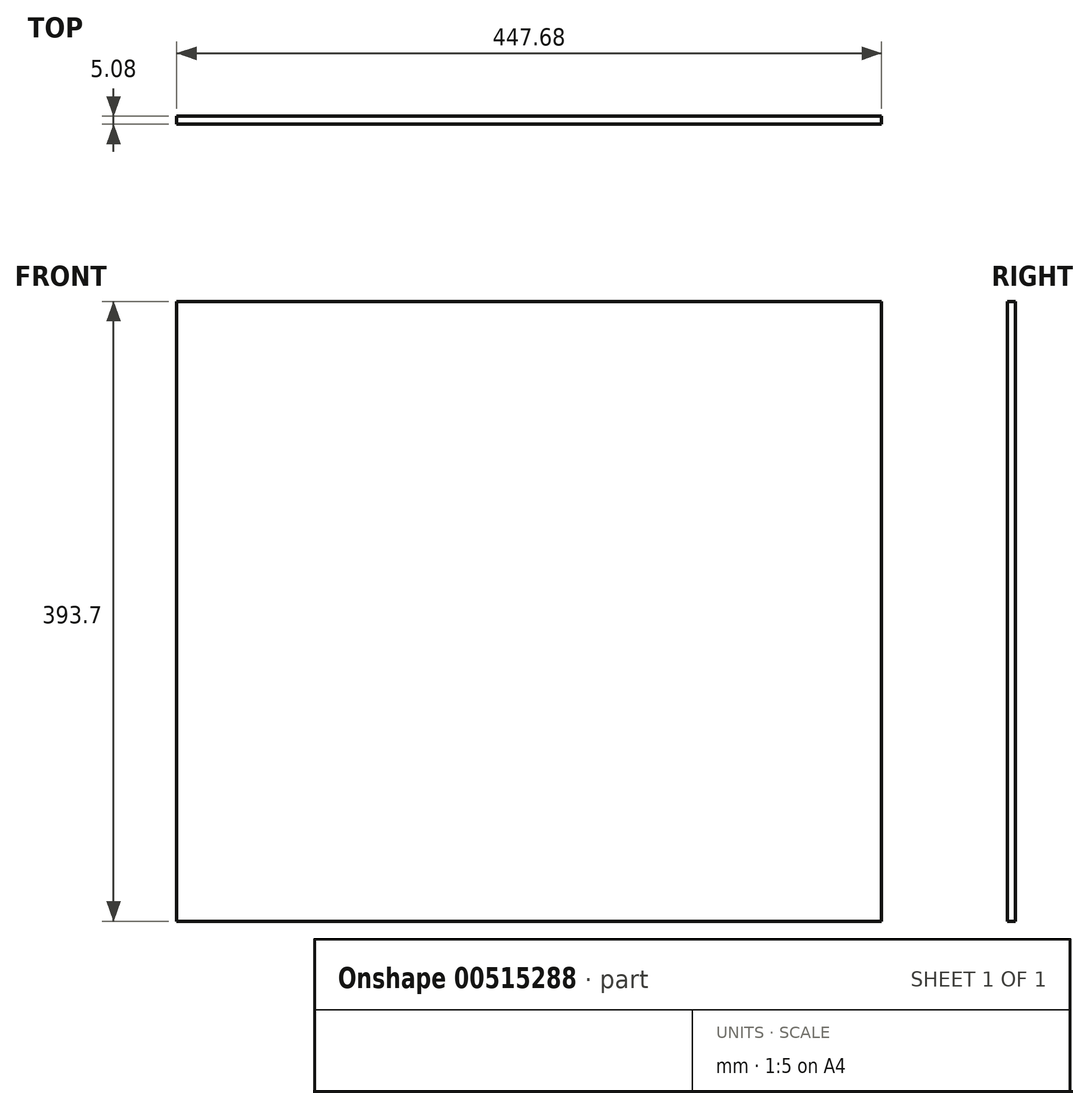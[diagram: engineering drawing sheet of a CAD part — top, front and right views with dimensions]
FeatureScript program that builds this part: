
annotation { "Feature Type Name" : "Feature", "Feature Type Description" : "" }
export const myFeature = defineFeature(function(context is Context, id is Id, definition is map)
    precondition{}
    {
        {
            var Q0;
            Q0=qCreatedBy(makeId("Front.planeOp"),FACE);
            var sketch = newSketch(context, id + "F0", { "sketchPlane" : qUnion([Q0])});
            skLineSegment(sketch, "E0.bottom", {"start": v(-525.36, 360.57) * mm, "end": v(-77.68, 360.57) * mm});
            skLineSegment(sketch, "E0.top", {"start": v(-525.36, -33.13) * mm, "end": v(-77.68, -33.13) * mm});
            skLineSegment(sketch, "E0.left", {"start": v(-525.36, 360.57) * mm, "end": v(-525.36, -33.13) * mm});
            skLineSegment(sketch, "E0.right", {"start": v(-77.68, 360.57) * mm, "end": v(-77.68, -33.13) * mm});
            skSolve(sketch);
        }
        {
            var Q0;
            Q0=makeQuery(id+"F0.imprint","IMPRINT",FACE,{"disambiguationData":[TD([[makeQuery(id+"F0.imprint","IMPRINT",EDGE,{"derivedFrom":sQuery(id+"F0.wireOp",EDGE,"E0.bottom")}),-1.0]])]});
            extrude(context, id + "F1", {"entities" : qUnion([Q0]), "depth" : 5.08 * mm, "offsetDistance" : 25.4 * mm});
        }
    });
